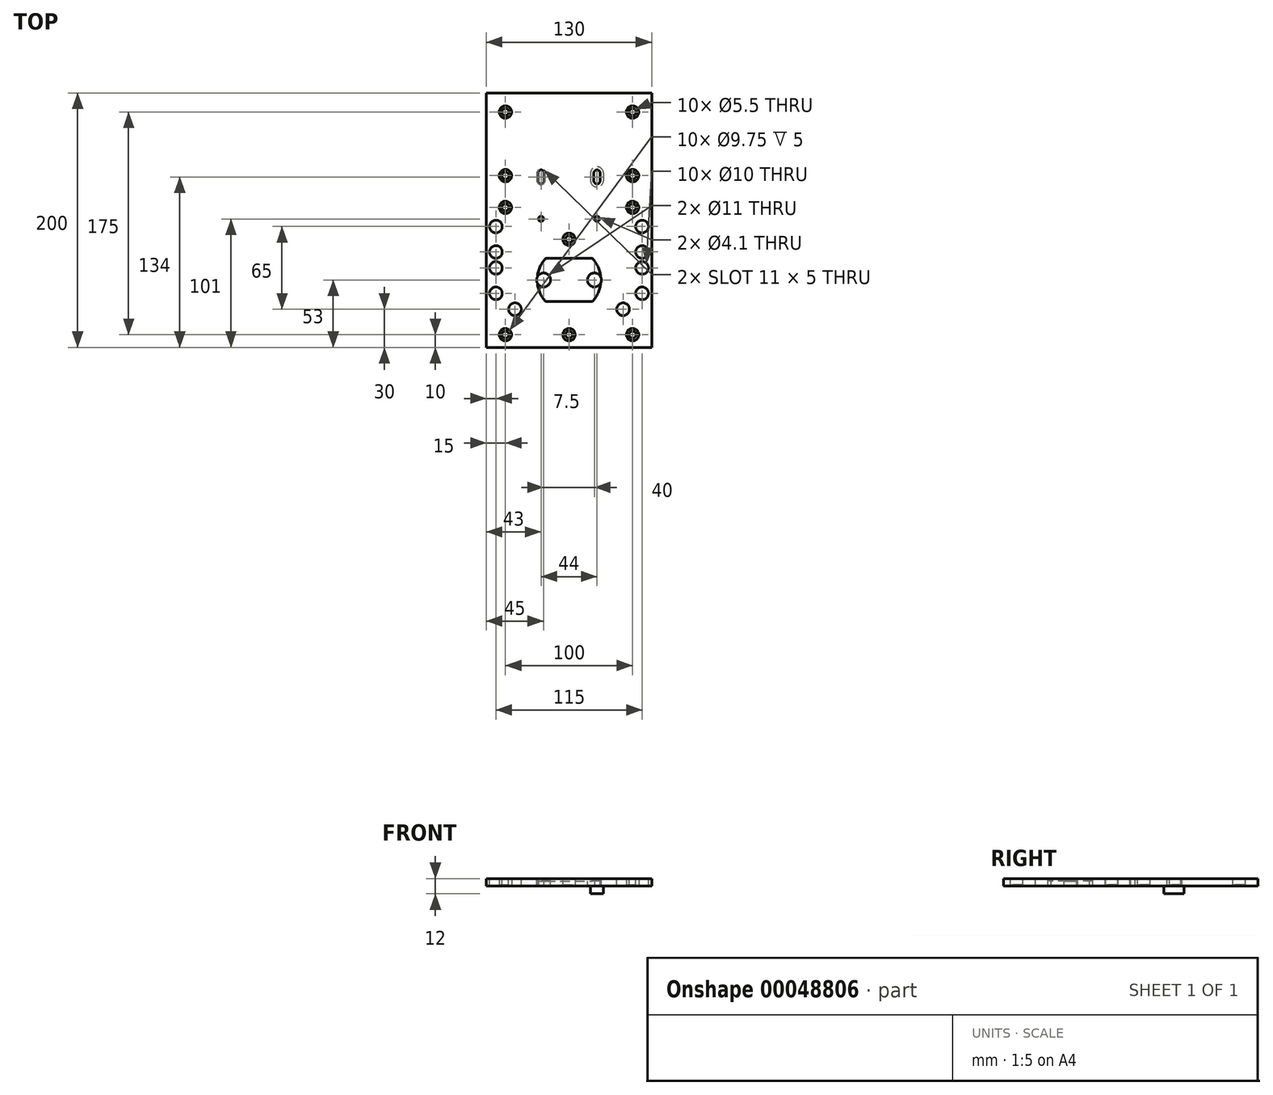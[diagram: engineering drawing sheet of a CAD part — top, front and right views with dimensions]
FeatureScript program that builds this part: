
annotation { "Feature Type Name" : "Feature", "Feature Type Description" : "" }
export const myFeature = defineFeature(function(context is Context, id is Id, definition is map)
    precondition{}
    {
        {
            var Q0;
            Q0=qCreatedBy(makeId("Top.planeOp"),FACE);
            var sketch = newSketch(context, id + "F0", { "sketchPlane" : qUnion([Q0])});
            skLineSegment(sketch, "E0.bottom", {"start": v(65, -100) * mm, "end": v(-65, -100) * mm});
            skLineSegment(sketch, "E0.top", {"start": v(65, 100) * mm, "end": v(-65, 100) * mm});
            skLineSegment(sketch, "E0.left", {"start": v(65, -100) * mm, "end": v(65, 100) * mm});
            skLineSegment(sketch, "E0.right", {"start": v(-65, -100) * mm, "end": v(-65, 100) * mm});
            skPoint(sketch, "E0.middle", {"position": v(0, 0) * mm});
            skSolve(sketch);
        }
        {
            var Q0;
            Q0=makeQuery(id+"F0.imprint","IMPRINT",FACE,{"disambiguationData":[TD([[makeQuery(id+"F0.imprint","IMPRINT",EDGE,{"derivedFrom":sQuery(id+"F0.wireOp",EDGE,"E0.bottom")}),-1.0]])]});
            extrude(context, id + "F1", {"entities" : qUnion([Q0]), "depth" : 12 * mm});
        }
        {
            var Q0;
            Q0=makeQuery(id+"F1.opExtrude","CAP_FACE",FACE,{"disambiguationData":[OSD([sQuery(id+"F0.wireOp",EDGE,"E0.bottom"),sQuery(id+"F0.wireOp",EDGE,"E0.top"),sQuery(id+"F0.wireOp",EDGE,"E0.left"),sQuery(id+"F0.wireOp",EDGE,"E0.right")])],"isStart":false});
            var sketch = newSketch(context, id + "F2", { "sketchPlane" : qUnion([Q0])});
            skPoint(sketch, "E1", {"position": v(-50, -90) * mm});
            skPoint(sketch, "E2.1.0.0", {"position": v(0, -90) * mm});
            skPoint(sketch, "E2.2.0.0", {"position": v(50, -90) * mm});
            skLineSegment(sketch, "E2.direction1", {"start": v(-50, -90) * mm, "end": v(0, -90) * mm, "construction": true});
            skPoint(sketch, "E3", {"position": v(0, -15) * mm});
            skPoint(sketch, "E4", {"position": v(-50, 10) * mm});
            skPoint(sketch, "E5.0.1.0", {"position": v(-50, 35) * mm});
            skPoint(sketch, "E5.1.0.0", {"position": v(50, 10) * mm});
            skPoint(sketch, "E5.1.1.0", {"position": v(50, 35) * mm});
            skPoint(sketch, "E5.2.0.0", {"position": v(150, 10) * mm});
            skPoint(sketch, "E5.2.1.0", {"position": v(150, 35) * mm});
            skLineSegment(sketch, "E5.direction1", {"start": v(-50, 10) * mm, "end": v(50, 10) * mm, "construction": true});
            skLineSegment(sketch, "E5.direction2", {"start": v(-50, 10) * mm, "end": v(-50, 35) * mm, "construction": true});
            skPoint(sketch, "E6", {"position": v(-50, 85) * mm});
            skPoint(sketch, "E7.MirrorP", {"position": v(50, 85) * mm});
            skSolve(sketch);
        }
        {
            var Q0;
            Q0=sQuery(id+"F2.wireOp",VERTEX,"E1");
            var Q1;
            Q1=sQuery(id+"F2.wireOp",VERTEX,"E2.1.0.0");
            var Q2;
            Q2=sQuery(id+"F2.wireOp",VERTEX,"E2.2.0.0");
            var Q3;
            Q3=sQuery(id+"F2.wireOp",VERTEX,"E4");
            var Q4;
            Q4=sQuery(id+"F2.wireOp",VERTEX,"E5.0.1.0");
            var Q5;
            Q5=sQuery(id+"F2.wireOp",VERTEX,"E5.1.0.0");
            var Q6;
            Q6=sQuery(id+"F2.wireOp",VERTEX,"E5.1.1.0");
            var Q7;
            Q7=sQuery(id+"F2.wireOp",VERTEX,"E6");
            var Q8;
            Q8=sQuery(id+"F2.wireOp",VERTEX,"E7.MirrorP");
            var Q9;
            Q9=sQuery(id+"F2.wireOp",VERTEX,"E3");
            var Q10;
            Q10=makeQuery(id+"F1.opExtrude","SWEPT_BODY",BODY,{"disambiguationData":[OSD([sQuery(id+"F0.wireOp",EDGE,"E0.bottom"),sQuery(id+"F0.wireOp",EDGE,"E0.top"),sQuery(id+"F0.wireOp",EDGE,"E0.left"),sQuery(id+"F0.wireOp",EDGE,"E0.right")])]});
            hole(context, id + "F3", {"style" : HoleStyle.C_BORE, "endStyle" : HoleEndStyle.THROUGH, "standardTappedOrClearance" : lookupTablePath({ "standard" : "ISO", "fit" : "Normal", "size" : "M5", "type" : "Clearance" }), "standardBlindInLast" : lookupTablePath({ "fit" : "Standard", "standard" : "ISO", "size" : "M5", "type" : "Clearance" }), "holeDiameter" : 5.5 * mm, "cBoreDiameter" : 9.75 * mm, "cBoreDepth" : 5 * mm, "locations" : qUnion([Q0, Q1, Q2, Q3, Q4, Q5, Q6, Q7, Q8, Q9]), "scope" : qUnion([Q10]), "isTappedThrough" : true, "startStyle" : HoleStartStyle.PART});
        }
        {
            var Q0;
            Q0=makeQuery(id+"F1.opExtrude","CAP_FACE",FACE,{"disambiguationData":[OSD([sQuery(id+"F0.wireOp",EDGE,"E0.bottom"),sQuery(id+"F0.wireOp",EDGE,"E0.top"),sQuery(id+"F0.wireOp",EDGE,"E0.left"),sQuery(id+"F0.wireOp",EDGE,"E0.right")])],"isStart":false});
            var sketch = newSketch(context, id + "F4", { "sketchPlane" : qUnion([Q0])});
            skPoint(sketch, "E8", {"position": v(-22, 37) * mm});
            skLineSegment(sketch, "E9", {"start": v(-22, 37) * mm, "end": v(-22, 31) * mm});
            skLineSegment(sketch, "E10.0", {"start": v(-24.5, 37) * mm, "end": v(-24.5, 31) * mm});
            skLineSegment(sketch, "E11.0", {"start": v(-19.5, 37) * mm, "end": v(-19.5, 31) * mm});
            skLineSegment(sketch, "E12.0", {"start": v(70, -105) * mm, "end": v(70, 105) * mm});
            skLineSegment(sketch, "E12.1", {"start": v(-70, -105) * mm, "end": v(70, -105) * mm});
            skLineSegment(sketch, "E12.2", {"start": v(-70, 105) * mm, "end": v(-70, -105) * mm});
            skLineSegment(sketch, "E12.3", {"start": v(70, 105) * mm, "end": v(-70, 105) * mm});
            skArc(sketch, "E13", {"start": v(-24.5, 37) * mm, "mid": v(-22, 39.5) * mm, "end": v(-19.5, 37) * mm});
            skArc(sketch, "E14", {"start": v(-19.5, 31) * mm, "mid": v(-22, 28.5) * mm, "end": v(-24.5, 31) * mm});
            skLineSegment(sketch, "E15.MirrorCS", {"start": v(19.5, 37) * mm, "end": v(19.5, 31) * mm});
            skArc(sketch, "E16.MirrorCS", {"start": v(24.5, 37) * mm, "mid": v(22, 39.5) * mm, "end": v(19.5, 37) * mm});
            skLineSegment(sketch, "E17.MirrorCS", {"start": v(24.5, 37) * mm, "end": v(24.5, 31) * mm});
            skArc(sketch, "E18.MirrorCS", {"start": v(19.5, 31) * mm, "mid": v(22, 28.5) * mm, "end": v(24.5, 31) * mm});
            skSolve(sketch);
        }
        {
            var Q0;
            Q0=makeQuery(id+"F4.imprint","IMPRINT",FACE,{"disambiguationData":[TD([[makeQuery(id+"F4.imprint","IMPRINT",EDGE,{"derivedFrom":sQuery(id+"F4.wireOp",EDGE,"E10.0")}),1.0]])]});
            var Q1;
            Q1=makeQuery(id+"F4.imprint","IMPRINT",FACE,{"disambiguationData":[TD([[makeQuery(id+"F4.imprint","IMPRINT",EDGE,{"derivedFrom":sQuery(id+"F4.wireOp",EDGE,"E15.MirrorCS")}),1.0]])]});
            extrude(context, id + "F5", {"entities" : qUnion([Q0, Q1]), "operationType" : NewBodyOperationType.REMOVE, "oppositeDirection" : true, "depth" : 25 * mm});
        }
        {
            var Q0;
            Q0=makeQuery(id+"F1.opExtrude","CAP_FACE",FACE,{"disambiguationData":[OSD([sQuery(id+"F0.wireOp",EDGE,"E0.bottom"),sQuery(id+"F0.wireOp",EDGE,"E0.top"),sQuery(id+"F0.wireOp",EDGE,"E0.left"),sQuery(id+"F0.wireOp",EDGE,"E0.right")])],"isStart":true});
            var sketch = newSketch(context, id + "F6", { "sketchPlane" : qUnion([Q0])});
            skArc(sketch, "E19.0", {"start": v(27, -37) * mm, "mid": v(22, -42) * mm, "end": v(17, -37) * mm});
            skLineSegment(sketch, "E19.1", {"start": v(27, -37) * mm, "end": v(27, -31) * mm});
            skArc(sketch, "E19.2", {"start": v(17, -31) * mm, "mid": v(22, -26) * mm, "end": v(27, -31) * mm});
            skLineSegment(sketch, "E19.3", {"start": v(17, -37) * mm, "end": v(17, -31) * mm});
            skArc(sketch, "E20.0", {"start": v(-27, -37) * mm, "mid": v(-22, -42) * mm, "end": v(-17, -37) * mm});
            skLineSegment(sketch, "E20.1", {"start": v(-27, -37) * mm, "end": v(-27, -31) * mm});
            skArc(sketch, "E20.2", {"start": v(-17, -31) * mm, "mid": v(-22, -26) * mm, "end": v(-27, -31) * mm});
            skLineSegment(sketch, "E20.3", {"start": v(-17, -37) * mm, "end": v(-17, -31) * mm});
            skSolve(sketch);
        }
        {
            var Q0;
            Q0=makeQuery(id+"F6.imprint","IMPRINT",FACE,{"disambiguationData":[TD([[makeQuery(id+"F6.imprint","IMPRINT",EDGE,{"derivedFrom":sQuery(id+"F6.wireOp",EDGE,"E19.0")}),-1.0]])]});
            var Q1;
            Q1=makeQuery(id+"F6.imprint","IMPRINT",FACE,{"disambiguationData":[TD([[makeQuery(id+"F6.imprint","IMPRINT",EDGE,{"derivedFrom":sQuery(id+"F6.wireOp",EDGE,"E20.0")}),1.0]])]});
            extrude(context, id + "F7", {"entities" : qUnion([Q0, Q1]), "operationType" : NewBodyOperationType.REMOVE, "oppositeDirection" : true, "depth" : 6 * mm});
        }
        {
            var Q0;
            Q0=makeQuery(id+"F1.opExtrude","CAP_FACE",FACE,{"disambiguationData":[OSD([sQuery(id+"F0.wireOp",EDGE,"E0.bottom"),sQuery(id+"F0.wireOp",EDGE,"E0.top"),sQuery(id+"F0.wireOp",EDGE,"E0.left"),sQuery(id+"F0.wireOp",EDGE,"E0.right")])],"isStart":false});
            var sketch = newSketch(context, id + "F8", { "sketchPlane" : qUnion([Q0])});
            skPoint(sketch, "E21", {"position": v(0, -47) * mm});
            skLineSegment(sketch, "E22", {"start": v(-65, -30) * mm, "end": v(65, -30) * mm, "construction": true});
            skLineSegment(sketch, "E23", {"start": v(-65, -64) * mm, "end": v(65, -64) * mm, "construction": true});
            skArc(sketch, "E24", {"start": v(18.33, -64) * mm, "mid": v(25, -47) * mm, "end": v(18.33, -30) * mm});
            skArc(sketch, "E25", {"start": v(-18.33, -64) * mm, "mid": v(-25, -47) * mm, "end": v(-18.33, -30) * mm});
            skLineSegment(sketch, "E26", {"start": v(-18.33, -30) * mm, "end": v(18.33, -30) * mm});
            skLineSegment(sketch, "E27", {"start": v(-18.33, -64) * mm, "end": v(18.33, -64) * mm});
            skSolve(sketch);
        }
        {
            var Q0;
            Q0=makeQuery(id+"F8.imprint","IMPRINT",FACE,{"disambiguationData":[TD([[makeQuery(id+"F8.imprint","IMPRINT",EDGE,{"derivedFrom":sQuery(id+"F8.wireOp",EDGE,"E24")}),1.0]])]});
            extrude(context, id + "F9", {"entities" : qUnion([Q0]), "operationType" : NewBodyOperationType.REMOVE, "oppositeDirection" : true, "depth" : 2 * mm});
        }
        {
            var Q0;
            Q0=makeQuery(id+"F1.opExtrude","CAP_FACE",FACE,{"disambiguationData":[OSD([sQuery(id+"F0.wireOp",EDGE,"E0.bottom"),sQuery(id+"F0.wireOp",EDGE,"E0.top"),sQuery(id+"F0.wireOp",EDGE,"E0.left"),sQuery(id+"F0.wireOp",EDGE,"E0.right")])],"isStart":true});
            var sketch = newSketch(context, id + "F10", { "sketchPlane" : qUnion([Q0])});
            skPoint(sketch, "E28", {"position": v(0, 47) * mm});
            skPoint(sketch, "E29", {"position": v(-20, 47) * mm});
            skPoint(sketch, "E30.MirrorP", {"position": v(20, 47) * mm});
            skSolve(sketch);
        }
        {
            var Q0;
            Q0=sQuery(id+"F10.wireOp",VERTEX,"E30.MirrorP");
            var Q1;
            Q1=sQuery(id+"F10.wireOp",VERTEX,"E29");
            var Q2;
            Q2=makeQuery(id+"F1.opExtrude","SWEPT_BODY",BODY,{"disambiguationData":[OSD([sQuery(id+"F0.wireOp",EDGE,"E0.bottom"),sQuery(id+"F0.wireOp",EDGE,"E0.top"),sQuery(id+"F0.wireOp",EDGE,"E0.left"),sQuery(id+"F0.wireOp",EDGE,"E0.right")])]});
            hole(context, id + "F11", {"style" : HoleStyle.C_BORE, "endStyle" : HoleEndStyle.THROUGH, "holeDiameter" : 5.1 * mm, "cBoreDiameter" : 11 * mm, "cBoreDepth" : 6 * mm, "locations" : qUnion([Q0, Q1]), "scope" : qUnion([Q2]), "isTappedThrough" : true, "startStyle" : HoleStartStyle.PART});
        }
        {
            var Q0;
            Q0=makeQuery(id+"F1.opExtrude","CAP_FACE",FACE,{"disambiguationData":[OSD([sQuery(id+"F0.wireOp",EDGE,"E0.bottom"),sQuery(id+"F0.wireOp",EDGE,"E0.top"),sQuery(id+"F0.wireOp",EDGE,"E0.left"),sQuery(id+"F0.wireOp",EDGE,"E0.right")])],"isStart":true});
            var sketch = newSketch(context, id + "F12", { "sketchPlane" : qUnion([Q0])});
            skPoint(sketch, "E31", {"position": v(57.5, 57.5) * mm});
            skPoint(sketch, "E32.0.1.0", {"position": v(57.5, 37.5) * mm});
            skPoint(sketch, "E32.1.0.0", {"position": v(-57.5, 57.5) * mm});
            skPoint(sketch, "E32.1.1.0", {"position": v(-57.5, 37.5) * mm});
            skLineSegment(sketch, "E32.direction1", {"start": v(57.5, 57.5) * mm, "end": v(-57.5, 57.5) * mm, "construction": true});
            skLineSegment(sketch, "E32.direction2", {"start": v(57.5, 57.5) * mm, "end": v(57.5, 37.5) * mm, "construction": true});
            skPoint(sketch, "E33", {"position": v(57.5, 25) * mm});
            skPoint(sketch, "E34.0.1.0", {"position": v(57.5, 5) * mm});
            skPoint(sketch, "E34.1.0.0", {"position": v(-57.5, 25) * mm});
            skPoint(sketch, "E34.1.1.0", {"position": v(-57.5, 5) * mm});
            skLineSegment(sketch, "E34.direction1", {"start": v(57.5, 25) * mm, "end": v(-57.5, 25) * mm, "construction": true});
            skLineSegment(sketch, "E34.direction2", {"start": v(57.5, 25) * mm, "end": v(57.5, 5) * mm, "construction": true});
            skPoint(sketch, "E35", {"position": v(-42.5, 70) * mm});
            skPoint(sketch, "E36.MirrorP", {"position": v(42.5, 70) * mm});
            skSolve(sketch);
        }
        {
            var Q0;
            Q0=sQuery(id+"F12.wireOp",VERTEX,"E31");
            var Q1;
            Q1=sQuery(id+"F12.wireOp",VERTEX,"E32.0.1.0");
            var Q2;
            Q2=sQuery(id+"F12.wireOp",VERTEX,"E32.1.0.0");
            var Q3;
            Q3=sQuery(id+"F12.wireOp",VERTEX,"E32.1.1.0");
            var Q4;
            Q4=sQuery(id+"F12.wireOp",VERTEX,"E33");
            var Q5;
            Q5=sQuery(id+"F12.wireOp",VERTEX,"E34.0.1.0");
            var Q6;
            Q6=sQuery(id+"F12.wireOp",VERTEX,"E34.1.0.0");
            var Q7;
            Q7=sQuery(id+"F12.wireOp",VERTEX,"E34.1.1.0");
            var Q8;
            Q8=sQuery(id+"F12.wireOp",VERTEX,"E35");
            var Q9;
            Q9=sQuery(id+"F12.wireOp",VERTEX,"E36.MirrorP");
            var Q10;
            Q10=makeQuery(id+"F1.opExtrude","SWEPT_BODY",BODY,{"disambiguationData":[OSD([sQuery(id+"F0.wireOp",EDGE,"E0.bottom"),sQuery(id+"F0.wireOp",EDGE,"E0.top"),sQuery(id+"F0.wireOp",EDGE,"E0.left"),sQuery(id+"F0.wireOp",EDGE,"E0.right")])]});
            hole(context, id + "F13", {"style" : HoleStyle.C_BORE, "endStyle" : HoleEndStyle.THROUGH, "holeDiameter" : 5 * mm, "cBoreDiameter" : 10 * mm, "cBoreDepth" : 6 * mm, "locations" : qUnion([Q0, Q1, Q2, Q3, Q4, Q5, Q6, Q7, Q8, Q9]), "scope" : qUnion([Q10]), "isTappedThrough" : true, "startStyle" : HoleStartStyle.PART});
        }
        {
            var Q0;
            Q0=makeQuery(id+"F1.opExtrude","CAP_FACE",FACE,{"disambiguationData":[OSD([sQuery(id+"F0.wireOp",EDGE,"E0.bottom"),sQuery(id+"F0.wireOp",EDGE,"E0.top"),sQuery(id+"F0.wireOp",EDGE,"E0.left"),sQuery(id+"F0.wireOp",EDGE,"E0.right")])],"isStart":false});
            var sketch = newSketch(context, id + "F14", { "sketchPlane" : qUnion([Q0])});
            skPoint(sketch, "E37", {"position": v(22, 1) * mm});
            skPoint(sketch, "E37.positionSnap0", {"position": v(22, 28.5) * mm});
            skPoint(sketch, "E38.MirrorP", {"position": v(-22, 1) * mm});
            skSolve(sketch);
        }
        {
            var Q0;
            Q0=sQuery(id+"F14.wireOp",VERTEX,"E37");
            var Q1;
            Q1=sQuery(id+"F14.wireOp",VERTEX,"E38.MirrorP");
            var Q2;
            Q2=makeQuery(id+"F1.opExtrude","SWEPT_BODY",BODY,{"disambiguationData":[OSD([sQuery(id+"F0.wireOp",EDGE,"E0.bottom"),sQuery(id+"F0.wireOp",EDGE,"E0.top"),sQuery(id+"F0.wireOp",EDGE,"E0.left"),sQuery(id+"F0.wireOp",EDGE,"E0.right")])]});
            hole(context, id + "F15", {"style" : HoleStyle.SIMPLE, "endStyle" : HoleEndStyle.THROUGH, "standardTappedOrClearance" : lookupTablePath({ "standard" : "ISO", "engagement" : "75%", "pitch" : "0.9 mm", "size" : "M5", "type" : "Tapped" }), "standardBlindInLast" : lookupTablePath({ "standard" : "ISO", "engagement" : "75%", "pitch" : "0.9 mm", "size" : "M5", "type" : "Tapped" }), "holeDiameter" : 4.1 * mm, "locations" : qUnion([Q0, Q1]), "scope" : qUnion([Q2]), "isTappedThrough" : true, "showTappedDepth" : true, "startStyle" : HoleStartStyle.PART});
        }
    });
